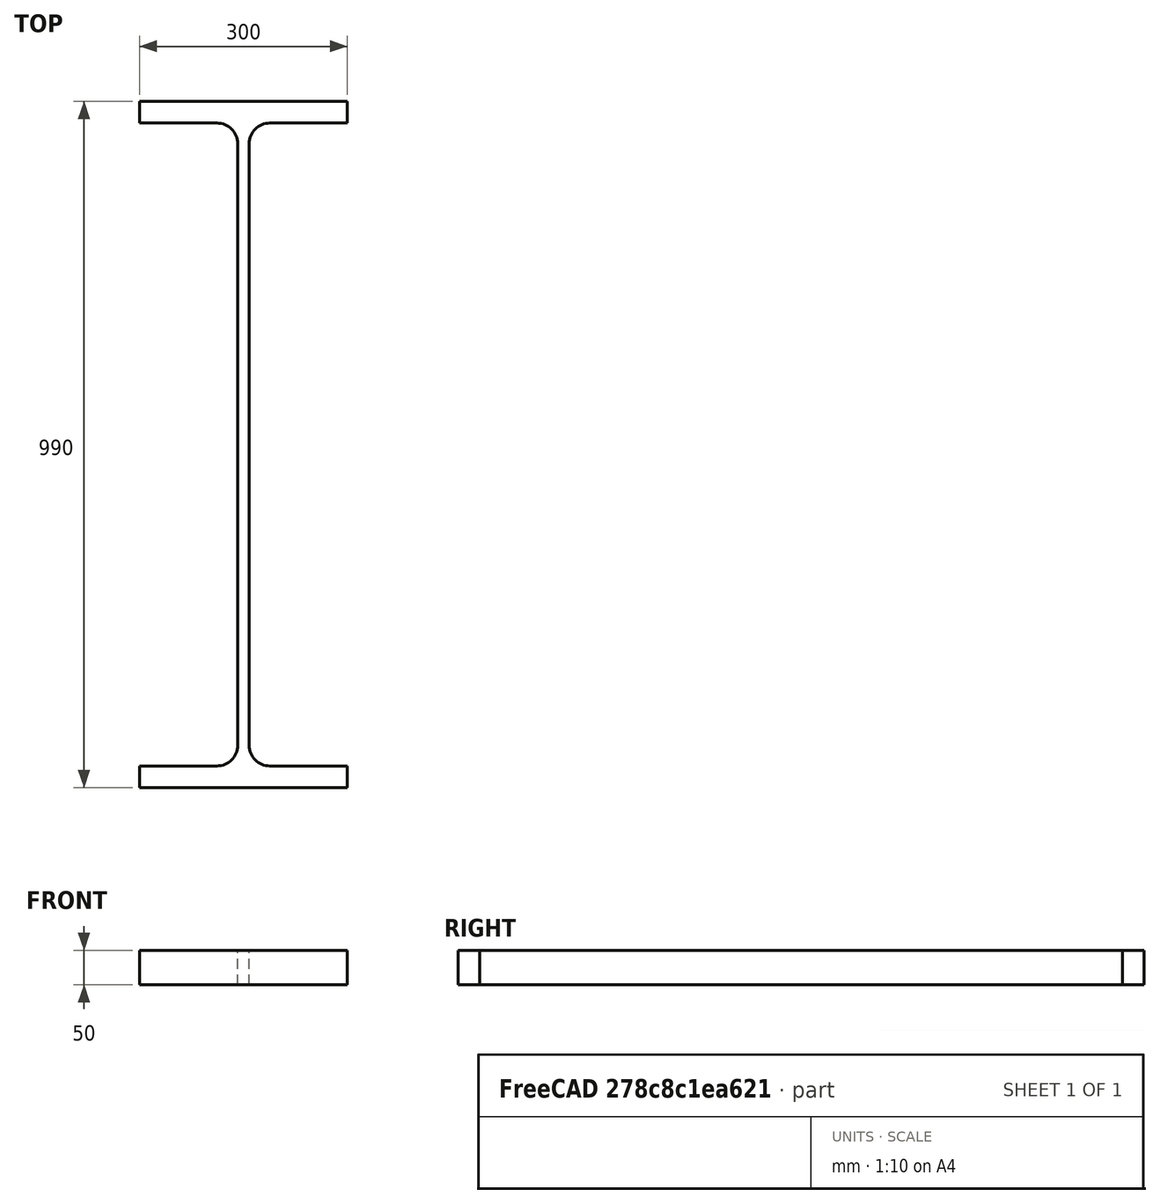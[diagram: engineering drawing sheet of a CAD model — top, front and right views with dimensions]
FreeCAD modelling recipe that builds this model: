
FCSTD DOCUMENT  (FreeCAD 0.15R4671 (Git))
Label: HE-A-Profile 1000 DIN1025-3 S235JR
License: All rights reserved
LicenseURL: http://en.wikipedia.org/wiki/All_rights_reserved
objects: Sketcher::SketchObject×1, Part::Extrusion×1
note: 2 computed .brp shape members not serialized (recipe doc carries the construction recipe); baked Part::Feature solids carry a one-line shape summary decoded from their .brp

FEATURE [Sketcher::SketchObject] Sketch
  sketch-geometry (16):
    g0: LineSegment StartX=8.25 StartY=-434 StartZ=0 EndX=8.25 EndY=434 EndZ=0
    g1: LineSegment StartX=38.25 StartY=464 StartZ=0 EndX=150 EndY=464 EndZ=0
    g2: LineSegment StartX=150 StartY=464 StartZ=0 EndX=150 EndY=495 EndZ=0
    g3: LineSegment StartX=150 StartY=495 StartZ=0 EndX=-150 EndY=495 EndZ=0
    g4: LineSegment StartX=-150 StartY=495 StartZ=0 EndX=-150 EndY=464 EndZ=0
    g5: LineSegment StartX=-150 StartY=464 StartZ=0 EndX=-38.25 EndY=464 EndZ=0
    g6: LineSegment StartX=-8.25 StartY=434 StartZ=0 EndX=-8.25 EndY=-434 EndZ=0
    g7: LineSegment StartX=-38.25 StartY=-464 StartZ=0 EndX=-150 EndY=-464 EndZ=0
    g8: LineSegment StartX=-150 StartY=-464 StartZ=0 EndX=-150 EndY=-495 EndZ=0
    g9: LineSegment StartX=-150 StartY=-495 StartZ=0 EndX=150 EndY=-495 EndZ=0
    g10: LineSegment StartX=150 StartY=-495 StartZ=0 EndX=150 EndY=-464 EndZ=0
    g11: LineSegment StartX=150 StartY=-464 StartZ=0 EndX=38.25 EndY=-464 EndZ=0
    g12: ArcOfCircle CenterX=38.25 CenterY=434 CenterZ=0 NormalX=0 NormalY=0 NormalZ=1 Radius=30 StartAngle=1.5708 EndAngle=3.14159
    g13: ArcOfCircle CenterX=38.25 CenterY=-434 CenterZ=0 NormalX=0 NormalY=0 NormalZ=1 Radius=30 StartAngle=3.14159 EndAngle=4.71239
    g14: ArcOfCircle CenterX=-38.25 CenterY=434 CenterZ=0 NormalX=0 NormalY=0 NormalZ=1 Radius=30 StartAngle=0 EndAngle=1.5708
    g15: ArcOfCircle CenterX=-38.25 CenterY=-434 CenterZ=0 NormalX=0 NormalY=0 NormalZ=1 Radius=30 StartAngle=4.71239 EndAngle=6.28319
  constraints (42):
    c: Vertical(g0)
    c: Coincident(g2,g1)
    c: Vertical(g2)
    c: Coincident(g3,g2)
    c: Coincident(g4,g3)
    c: Vertical(g4)
    c: Coincident(g5,g4)
    c: Horizontal(g5)
    c: Vertical(g6)
    c: Horizontal(g7)
    c: Coincident(g8,g7)
    c: Vertical(g8)
    c: Coincident(g9,g8)
    c: Horizontal(g9)
    c: Coincident(g10,g9)
    c: Vertical(g10)
    c: Coincident(g11,g10)
    c: Horizontal(g11)
    c: Tangent(g1,g12) = 1.5708
    c: Tangent(g0,g12) = 1.5708
    c: Tangent(g0,g13) = 1.5708
    c: Tangent(g11,g13) = 1.5708
    c: Tangent(g5,g14) = 1.5708
    c: Tangent(g6,g14) = 1.5708
    c: Tangent(g6,g15) = 1.5708
    c: Tangent(g7,g15) = 1.5708
    c: Equal(g3,g9)
    c: Equal(g2,g4)
    c: Equal(g4,g8)
    c: Equal(g8,g10)
    c: Equal(g12,g14)
    c: Equal(g14,g15)
    c: Equal(g15,g13)
    c: Symmetric(g2,g3,g-2)
    c: Symmetric(g9,g8,g-2)
    c: Symmetric(g0,g6,g-2)
    c: Symmetric(g2,g9,g-1)
    c: DistanceY(g2,g9) = -990
    c: DistanceX(g3) = -300
    c: DistanceX(g0,g6) = -16.5
    c: DistanceY(g2) = 31
    c: Radius(g12) = 30
FEATURE [Part::Extrusion] Extrude  label="HE-A-Profile 1000 DIN1025-3 S235JR"
  Base = -> Sketch
  Dir = (0,0,50)
  Solid = true
